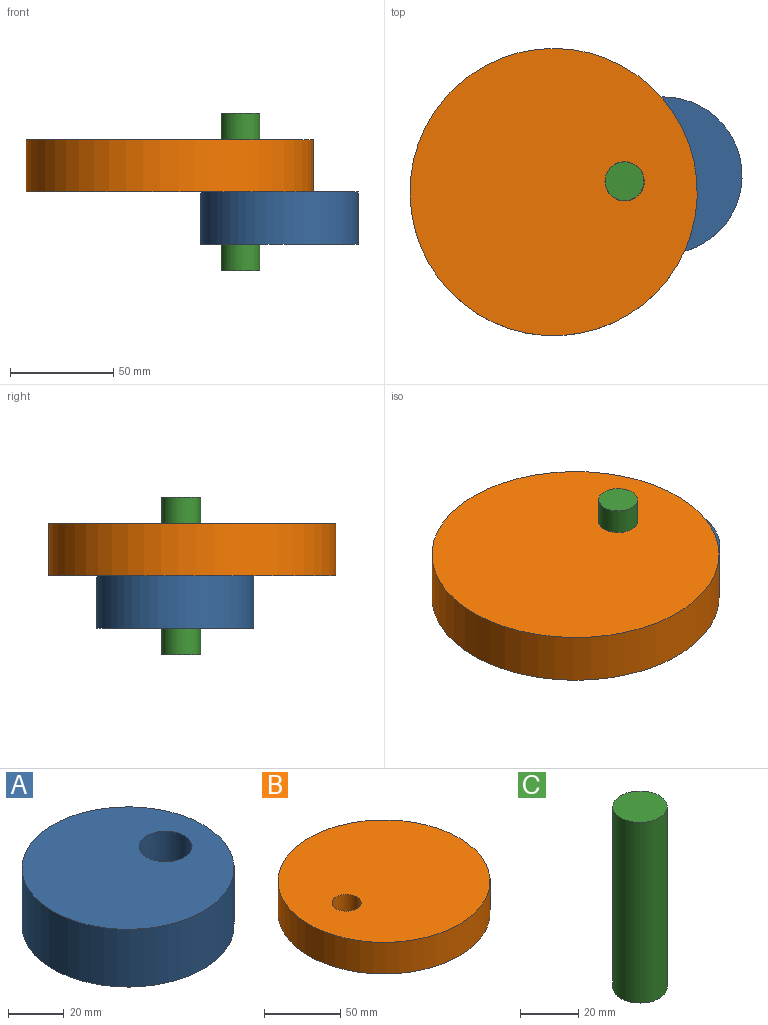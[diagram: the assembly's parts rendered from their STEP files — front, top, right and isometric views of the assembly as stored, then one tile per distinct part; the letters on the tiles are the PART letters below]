
ASSEMBLY  parts=3 mates=4
PART A: 4 faces, bbox 76.2x76.2x25.4 mm
  f0: cylinder r=38.1mm len=76.2mm, axis (0,0,-1), area 6080.5mm2, adj f1,f2
  f1: plane 76.2x76.2mm, normal (0,0,1), area 4275.3mm2, adj f0,f3
  f2: plane 76.2x76.2mm, normal (0,0,-1), area 4275.3mm2, adj f0,f3
  f3: cylinder r=9.53mm len=25.4mm, axis (0,0,1), area 1520.1mm2, adj f1,f2
PART B: 4 faces, bbox 139.3x139.3x25.4 mm
  f0: cylinder r=69.64mm len=139.28mm, axis (0,0,-1), area 11113.8mm2, adj f1,f2
  f1: plane 139.28x139.28mm, normal (0,0,1), area 14950.2mm2, adj f0,f3
  f2: plane 139.28x139.28mm, normal (0,0,-1), area 14950.2mm2, adj f0,f3
  f3: cylinder r=9.53mm len=25.4mm, axis (0,0,1), area 1520.1mm2, adj f1,f2
PART C: 3 faces, bbox 18.8x18.8x76.2 mm
  f0: cylinder r=9.4mm len=76.2mm, axis (0,0,-1), area 4499.6mm2, adj f1,f2
  f1: plane 18.8x18.8mm, normal (0,0,1), area 277.5mm2, adj f0
  f2: plane 18.8x18.8mm, normal (0,0,-1), area 277.5mm2, adj f0
PLACE A rot(axis=(0.08,-1,0),180deg) t=(-114.45,110.92,56.06)mm
PLACE B rot(axis=(0.08,-1,0),180deg) t=(-229.04,132.13,81.46)mm
PLACE C rot(axis=(0,0,1),8.6deg) t=(-71.58,165.95,17.96)mm
MATE pin_slot C.f0 <-> A.f3  axis (0,0,1) through (-133.29,108.06,94.16)mm
MATE fastened C.f0 <-> B.f3  axis (0,0,-1) through (-133.29,108.06,56.06)mm
MATE fastened A.f0 <-> B.f1  axis (0,0,1) through (-114.45,110.92,43.36)mm
MATE cylindrical A.f3 <-> B.f3  axis (0,0,1) through (-133.29,108.06,56.06)mm
